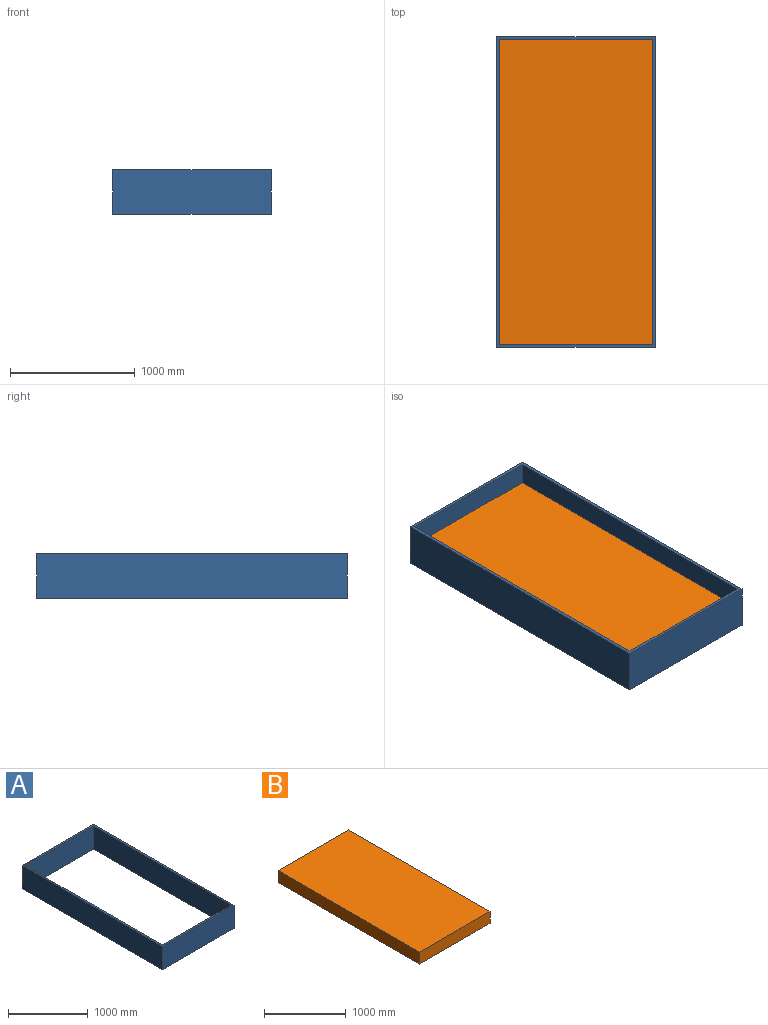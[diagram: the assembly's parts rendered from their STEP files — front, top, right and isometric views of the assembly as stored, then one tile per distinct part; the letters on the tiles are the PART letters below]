
ASSEMBLY  parts=2 mates=1
PART A: 10 faces, bbox 1270x2489.2x355.6 mm
  f0: plane 1270x355.6mm, normal (0,1,0), area 451612mm2, adj f1,f7,f8,f9
  f1: plane 2489.2x355.6mm, normal (-1,0,0), area 885159.5mm2, adj f0,f2,f8,f9
  f2: plane 1270x355.6mm, normal (0,-1,0), area 451612mm2, adj f1,f7,f8,f9
  f3: plane 2438.4x355.6mm, normal (1,0,0), area 867095mm2, adj f4,f6,f8,f9
  f4: plane 1219.2x355.6mm, normal (0,-1,0), area 433547.5mm2, adj f3,f5,f8,f9
  f5: plane 2438.4x355.6mm, normal (-1,0,0), area 867095mm2, adj f4,f6,f8,f9
  f6: plane 1219.2x355.6mm, normal (0,1,0), area 433547.5mm2, adj f3,f5,f8,f9
  f7: plane 2489.2x355.6mm, normal (1,0,0), area 885159.5mm2, adj f0,f2,f8,f9
  f8: plane 2489.2x1270mm, normal (0,0,1), area 188386.7mm2, adj f0,f1,f2,f3,f4,f5,f6,f7
  f9: plane 2489.2x1270mm, normal (0,0,-1), area 188386.7mm2, adj f0,f1,f2,f3,f4,f5,f6,f7
PART B: 6 faces, bbox 1219.2x2438.4x177.8 mm
  f0: plane 1219.2x177.8mm, normal (0,1,0), area 216773.8mm2, adj f1,f3,f4,f5
  f1: plane 2438.4x177.8mm, normal (-1,0,0), area 433547.5mm2, adj f0,f2,f4,f5
  f2: plane 1219.2x177.8mm, normal (0,-1,0), area 216773.8mm2, adj f1,f3,f4,f5
  f3: plane 2438.4x177.8mm, normal (1,0,0), area 433547.5mm2, adj f0,f2,f4,f5
  f4: plane 2438.4x1219.2mm, normal (0,0,1), area 2972897.3mm2, adj f0,f1,f2,f3
  f5: plane 2438.4x1219.2mm, normal (0,0,-1), area 2972897.3mm2, adj f0,f1,f2,f3
PLACE A t=(227.19,4816.77,0)mm
PLACE B t=(227.19,4816.77,0)mm
MATE fastened A.f9 <-> B.f5  axis (0,0,-1) through (609.6,1219.2,0)mm
